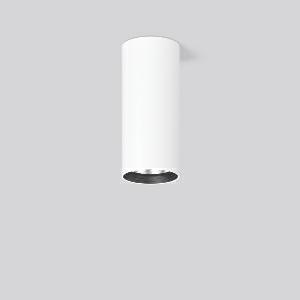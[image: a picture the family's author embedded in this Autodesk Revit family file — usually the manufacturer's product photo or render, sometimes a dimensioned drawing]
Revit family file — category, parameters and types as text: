
# Revit family: heledon_mini_a_931208_002_2_76_41fa
name_source: partatom
category: Lighting Fixtures
units: mm (PartAtom-declared; Revit-internal decimal feet)

## family parameters
Cut with Voids When Loaded = No
Host = Face
Light Source = No
Part Type = Normal
Room Calculation Point = No
Round Connector Dimension = Use Diameter
Shared = No

## types (1)
- HELEDON mini A (1 x LED Modul 927, 3400 lm, 2700)
    Apparent Load = 29 VA
    Approval mark = CE
    CIE Flux Codes = 100 100 100 100 100
    Color Rendering = 92
    Color Temperature = 2700
    Default Elevation = 1800 mm
    Description = Series: HELEDON mini
Cylindrical surface-mounted downlight. Housing: die-cast aluminium, powder-coated. Internal ceiling frame polycarbonate with bayonet mounting. Black plastic ring and recessed LED to prevent glare from the side. Optical assembly with reflector made of MIRO-Silver with 98% total light reflection for outstanding efficiency - can be changed without tools. Best colour rendering index Ra>90. Suitable for Ceiling mounting. Easy installation with a separate ceiling frame with bayonet mounting and plug connection. Driver integrated. Connected via plug-in connector. High quality converter without flickering and stroboscopic effect. The following accessories can be mounted without use of tools: interchangeable lenses, decorative glasses, honeycomb louvre, clear and frosted diffusers, white interchangeable plastic ring. 
Colour: traffic white, matt (RAL 9016)
Diameter: 87 mm
Height: 197 mm
Lamp: LED
Socket: without socket
Colour temperature: 2700K
Colour rendering index (CRI): 92
System power: 29 W
Rated luminous flux: 3400 lm
Luminous efficiency: 117 lm/W
Control gear: Converter, dimmable, DALI
Protection class: I
Type of protection: IP 20
    Height = 197 mm
    Lamp = 1 x LED Modul 927
    Lamp Light Flux = 3400 lm
    Lamp count = 1
    Length = 87 mm
    Lifetime = 50000 h
    Luminous efficacy = 117 lm/W
    Manufacturer = RZB
    ModVariant = No
    Model = 931208.002.2.76
    Mounting Place = Ceiling
    Mounting Type = Surface mounted
    Number of Poles = 1
    OnlyDefault = Yes
    Power Factor = 1
    Product Name = HELEDON mini A
    Product group = Surface mounted downlights
    ProductGroupID = 302
    Protection Class = Protection class I
    Protection Degree = IP 20
    RLX_Detail_Level = 1
    RLX_Emergency_Light_Flux = 0 lm
    RLX_Emergency_Type = 0
    RLX_Emergency_Type_DB = No
    RlxData = <blob elided: 105321 chars, md5=13b12f89>
    Socket = socket
    Standby Power = 0 W
    System Light Flux = 3400 lm
    System Power = 29 W
    Type Comments = Product without accessories
    Type Image = 931188.002.jpg
    URL = http://relux.com
    VarID = ---
    Voltage = 230 V
    Voltage Range = 220-240 V
    Weight = 0.00 kg
    Width = 0 mm  [stored 0 ft]

note: [stored X ft] marks values corroborated as IEEE doubles in the binary element streams (Revit-internal decimal feet)

## geometry (parser evidence)
native form markers: Blend x4, Sweep x10
no freeform markers — native parametric forms only
